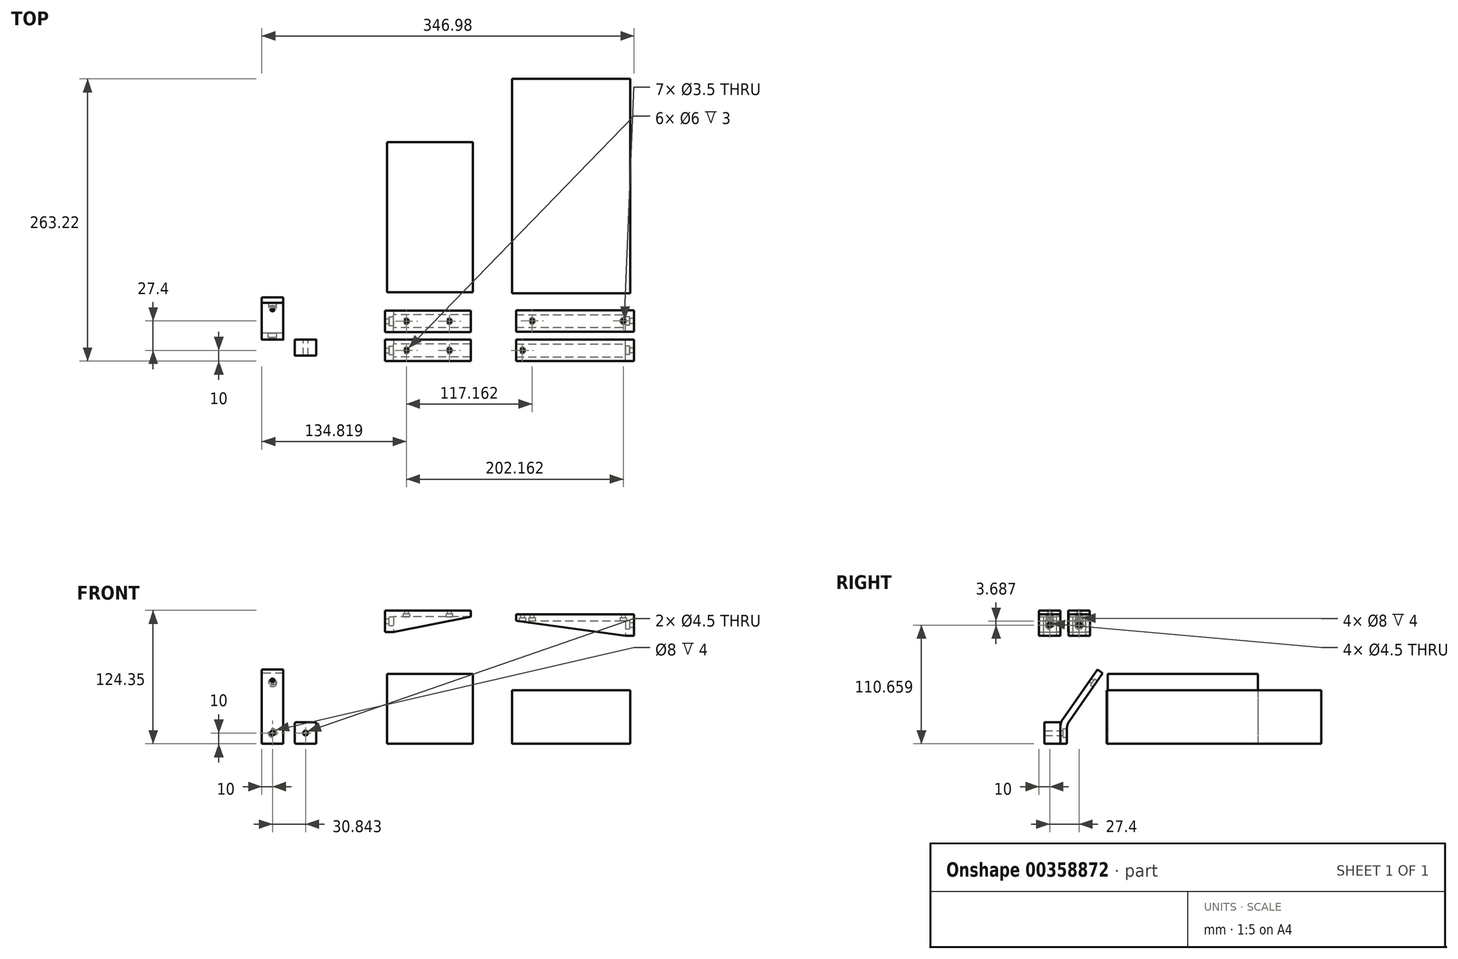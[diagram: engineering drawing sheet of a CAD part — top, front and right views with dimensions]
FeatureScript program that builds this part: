
annotation { "Feature Type Name" : "Feature", "Feature Type Description" : "" }
export const myFeature = defineFeature(function(context is Context, id is Id, definition is map)
    precondition{}
    {
        {
            var Q0;
            Q0=qCreatedBy(makeId("Right.planeOp"),FACE);
            var sketch = newSketch(context, id + "F0", { "sketchPlane" : qUnion([Q0])});
            skLineSegment(sketch, "E0", {"start": v(0, 0) * mm, "end": v(6, 0) * mm});
            skLineSegment(sketch, "E1", {"start": v(6, 0) * mm, "end": v(6, 18.1) * mm});
            skLineSegment(sketch, "E2", {"start": v(6, 18.1) * mm, "end": v(39.33, 65.7) * mm});
            skLineSegment(sketch, "E3", {"start": v(39.33, 65.7) * mm, "end": v(34.41, 69.15) * mm});
            skLineSegment(sketch, "E4", {"start": v(34.41, 69.15) * mm, "end": v(0, 20) * mm});
            skLineSegment(sketch, "E5", {"start": v(0, 20) * mm, "end": v(0, 0) * mm});
            skSolve(sketch);
        }
        {
            var Q0;
            Q0=makeQuery(id+"F0.imprint","IMPRINT",FACE,{"disambiguationData":[TD([[makeQuery(id+"F0.imprint","IMPRINT",EDGE,{"derivedFrom":sQuery(id+"F0.wireOp",EDGE,"E0")}),1.0]])]});
            extrude(context, id + "F1", {"entities" : qUnion([Q0]), "depth" : 20 * mm});
        }
        {
            var Q0;
            Q0=makeQuery(id+"F1.opExtrude","SWEPT_FACE",FACE,{"disambiguationData":[OSD([sQuery(id+"F0.wireOp",EDGE,"E1")])]});
            var sketch = newSketch(context, id + "F2", { "sketchPlane" : qUnion([Q0])});
            skCircle(sketch, "E6", {"center": v(-10, 10) * mm, "radius": 2.25 * mm});
            skPoint(sketch, "E6.centerSnap0", {"position": v(-10, 0) * mm});
            skCircle(sketch, "E7", {"center": v(-10, 10) * mm, "radius": 4 * mm});
            skSolve(sketch);
        }
        {
            var Q0;
            Q0=makeQuery(id+"F1.opExtrude","SWEPT_FACE",FACE,{"disambiguationData":[OSD([sQuery(id+"F0.wireOp",EDGE,"E4")])]});
            var sketch = newSketch(context, id + "F3", { "sketchPlane" : qUnion([Q0])});
            skCircle(sketch, "E8", {"center": v(10, 64.38) * mm, "radius": 1.75 * mm});
            skPoint(sketch, "E8.centerSnap0", {"position": v(10, 16.38) * mm});
            skCircle(sketch, "E9", {"center": v(10, 64.38) * mm, "radius": 3.5 * mm});
            skSolve(sketch);
        }
        {
            var Q0;
            Q0=makeQuery(id+"F3.imprint","IMPRINT",FACE,{"disambiguationData":[TD([[makeQuery(id+"F3.imprint","IMPRINT",EDGE,{"derivedFrom":sQuery(id+"F3.wireOp",EDGE,"E8")}),1.0]])]});
            extrude(context, id + "F4", {"entities" : qUnion([Q0]), "operationType" : NewBodyOperationType.REMOVE, "oppositeDirection" : true, "depth" : 25 * mm});
        }
        {
            var Q0;
            Q0=makeQuery(id+"F1.opExtrude","SWEPT_FACE",FACE,{"disambiguationData":[OSD([sQuery(id+"F0.wireOp",EDGE,"E2")])]});
            var sketch = newSketch(context, id + "F5", { "sketchPlane" : qUnion([Q0])});
            skCircle(sketch, "E10", {"center": v(-10, 64.38) * mm, "radius": 3.5 * mm});
            skSolve(sketch);
        }
        {
            var Q0;
            Q0=makeQuery(id+"F5.imprint","IMPRINT",FACE,{"disambiguationData":[TD([[makeQuery(id+"F5.imprint","IMPRINT",EDGE,{"derivedFrom":sQuery(id+"F5.wireOp",EDGE,"E10")}),1.0]])]});
            extrude(context, id + "F6", {"entities" : qUnion([Q0]), "operationType" : NewBodyOperationType.REMOVE, "oppositeDirection" : true, "depth" : 3 * mm});
        }
        {
            var Q0;
            Q0=makeQuery(id+"F2.imprint","IMPRINT",FACE,{"disambiguationData":[TD([[makeQuery(id+"F2.imprint","IMPRINT",EDGE,{"derivedFrom":sQuery(id+"F2.wireOp",EDGE,"E6")}),1.0]])]});
            extrude(context, id + "F7", {"entities" : qUnion([Q0]), "operationType" : NewBodyOperationType.REMOVE, "oppositeDirection" : true, "depth" : 25 * mm});
        }
        {
            var Q0;
            Q0=makeQuery(id+"F2.imprint","IMPRINT",FACE,{"disambiguationData":[TD([[makeQuery(id+"F2.imprint","IMPRINT",EDGE,{"derivedFrom":sQuery(id+"F2.wireOp",EDGE,"E6")}),-1.0]])]});
            extrude(context, id + "F8", {"entities" : qUnion([Q0]), "operationType" : NewBodyOperationType.REMOVE, "oppositeDirection" : true, "depth" : 4 * mm});
        }
        {
            var Q0;
            Q0=makeQuery(id+"F1.opExtrude","SWEPT_EDGE",EDGE,{"disambiguationData":[OSD([sQuery(id+"F0.wireOp",EDGE,"E1"),sQuery(id+"F0.wireOp",EDGE,"E2")])]});
            var Q1;
            Q1=makeQuery(id+"F1.opExtrude","SWEPT_EDGE",EDGE,{"disambiguationData":[OSD([sQuery(id+"F0.wireOp",EDGE,"E4"),sQuery(id+"F0.wireOp",EDGE,"E5")])]});
            fillet(context, id + "F9", {"entities" : qUnion([Q0, Q1]), "radius" : 13 * mm, "tangentPropagation" : true, "allowEdgeOverflow" : false});
        }
        {
            var Q0;
            Q0=qCreatedBy(makeId("Top.planeOp"),FACE);
            var sketch = newSketch(context, id + "F10", { "sketchPlane" : qUnion([Q0])});
            skLineSegment(sketch, "E11.bottom", {"start": v(116.68, 184.13) * mm, "end": v(196.68, 184.13) * mm});
            skLineSegment(sketch, "E11.top", {"start": v(116.68, 44.13) * mm, "end": v(196.68, 44.13) * mm});
            skLineSegment(sketch, "E11.left", {"start": v(116.68, 184.13) * mm, "end": v(116.68, 44.13) * mm});
            skLineSegment(sketch, "E11.right", {"start": v(196.68, 184.13) * mm, "end": v(196.68, 44.13) * mm});
            skSolve(sketch);
        }
        {
            var Q0;
            Q0=makeQuery(id+"F10.imprint","IMPRINT",FACE,{"disambiguationData":[TD([[makeQuery(id+"F10.imprint","IMPRINT",EDGE,{"derivedFrom":sQuery(id+"F10.wireOp",EDGE,"E11.bottom")}),-1.0]])]});
            extrude(context, id + "F11", {"entities" : qUnion([Q0]), "depth" : 65 * mm});
        }
        {
            var Q0;
            Q0=qCreatedBy(makeId("Top.planeOp"),FACE);
            var sketch = newSketch(context, id + "F12", { "sketchPlane" : qUnion([Q0])});
            skLineSegment(sketch, "E12.bottom", {"start": v(233.36, 43.22) * mm, "end": v(343.36, 43.22) * mm});
            skLineSegment(sketch, "E12.top", {"start": v(233.36, 243.22) * mm, "end": v(343.36, 243.22) * mm});
            skLineSegment(sketch, "E12.left", {"start": v(233.36, 43.22) * mm, "end": v(233.36, 243.22) * mm});
            skLineSegment(sketch, "E12.right", {"start": v(343.36, 43.22) * mm, "end": v(343.36, 243.22) * mm});
            skSolve(sketch);
        }
        {
            var Q0;
            Q0=makeQuery(id+"F12.imprint","IMPRINT",FACE,{"disambiguationData":[TD([[makeQuery(id+"F12.imprint","IMPRINT",EDGE,{"derivedFrom":sQuery(id+"F12.wireOp",EDGE,"E12.bottom")}),1.0]])]});
            extrude(context, id + "F13", {"entities" : qUnion([Q0]), "depth" : 50 * mm});
        }
        {
            var Q0;
            Q0=qCreatedBy(makeId("Front.planeOp"),FACE);
            var sketch = newSketch(context, id + "F14", { "sketchPlane" : qUnion([Q0])});
            skLineSegment(sketch, "E13", {"start": v(114.82, 104.35) * mm, "end": v(122.82, 104.35) * mm});
            skLineSegment(sketch, "E14", {"start": v(114.82, 104.35) * mm, "end": v(114.82, 124.35) * mm});
            skLineSegment(sketch, "E15", {"start": v(114.82, 124.35) * mm, "end": v(194.82, 124.35) * mm});
            skLineSegment(sketch, "E16", {"start": v(194.82, 124.35) * mm, "end": v(194.82, 118.35) * mm});
            skLineSegment(sketch, "E17", {"start": v(194.82, 118.35) * mm, "end": v(122.82, 118.35) * mm});
            skLineSegment(sketch, "E18", {"start": v(122.82, 118.35) * mm, "end": v(122.82, 104.35) * mm});
            skSolve(sketch);
        }
        {
            var Q0;
            Q0=makeQuery(id+"F14.imprint","IMPRINT",FACE,{"disambiguationData":[TD([[makeQuery(id+"F14.imprint","IMPRINT",EDGE,{"derivedFrom":sQuery(id+"F14.wireOp",EDGE,"E13")}),1.0]])]});
            extrude(context, id + "F15", {"entities" : qUnion([Q0]), "depth" : 20 * mm});
        }
        {
            var Q0;
            Q0=makeQuery(id+"F15.opExtrude","SWEPT_FACE",FACE,{"disambiguationData":[OSD([sQuery(id+"F14.wireOp",EDGE,"E18")])]});
            var sketch = newSketch(context, id + "F16", { "sketchPlane" : qUnion([Q0])});
            skCircle(sketch, "E19", {"center": v(-10, 114.35) * mm, "radius": 2.25 * mm});
            skPoint(sketch, "E19.centerSnap0", {"position": v(-10, 104.35) * mm});
            skCircle(sketch, "E20", {"center": v(-10, 114.35) * mm, "radius": 4 * mm});
            skSolve(sketch);
        }
        {
            var Q0;
            Q0=makeQuery(id+"F16.imprint","IMPRINT",FACE,{"disambiguationData":[TD([[makeQuery(id+"F16.imprint","IMPRINT",EDGE,{"derivedFrom":sQuery(id+"F16.wireOp",EDGE,"E19")}),1.0]])]});
            extrude(context, id + "F17", {"entities" : qUnion([Q0]), "operationType" : NewBodyOperationType.REMOVE, "endBound" : BoundingType.THROUGH_ALL, "oppositeDirection" : true, "depth" : 25 * mm});
        }
        {
            var Q0;
            Q0=makeQuery(id+"F16.imprint","IMPRINT",FACE,{"disambiguationData":[TD([[makeQuery(id+"F16.imprint","IMPRINT",EDGE,{"derivedFrom":sQuery(id+"F16.wireOp",EDGE,"E19")}),-1.0]])]});
            extrude(context, id + "F18", {"entities" : qUnion([Q0]), "operationType" : NewBodyOperationType.REMOVE, "oppositeDirection" : true, "depth" : 4 * mm});
        }
        {
            var Q0;
            Q0=makeQuery(id+"F15.opExtrude","CAP_VERTEX",VERTEX,{"disambiguationData":[OSD([sQuery(id+"F14.wireOp",EDGE,"E13"),sQuery(id+"F14.wireOp",EDGE,"E18")])],"isStart":false});
            var Q1;
            Q1=makeQuery(id+"F15.opExtrude","CAP_VERTEX",VERTEX,{"disambiguationData":[OSD([sQuery(id+"F14.wireOp",EDGE,"E13"),sQuery(id+"F14.wireOp",EDGE,"E18")])],"isStart":true});
            var Q2;
            Q2=makeQuery(id+"F15.opExtrude","CAP_VERTEX",VERTEX,{"disambiguationData":[OSD([sQuery(id+"F14.wireOp",EDGE,"E16"),sQuery(id+"F14.wireOp",EDGE,"E17")])],"isStart":false});
            cPlane(context, id + "F19", {"entities" : qUnion([Q0, Q1, Q2]), "cplaneType" : CPlaneType.THREE_POINT, "offset" : 25 * mm, "width" : 150 * mm, "height" : 150 * mm});
        }
        {
            var Q0;
            Q0=qCreatedBy(id+"F19.planeOp",FACE);
            var sketch = newSketch(context, id + "F20", { "sketchPlane" : qUnion([Q0])});
            skLineSegment(sketch, "E21.bottom", {"start": v(140.48, -20) * mm, "end": v(213.83, -20) * mm});
            skLineSegment(sketch, "E21.top", {"start": v(140.48, -16) * mm, "end": v(213.83, -16) * mm});
            skLineSegment(sketch, "E21.left", {"start": v(140.48, -20) * mm, "end": v(140.48, -16) * mm});
            skLineSegment(sketch, "E21.right", {"start": v(213.83, -20) * mm, "end": v(213.83, -16) * mm});
            skLineSegment(sketch, "E22.bottom", {"start": v(140.48, 0) * mm, "end": v(213.83, 0) * mm});
            skLineSegment(sketch, "E22.top", {"start": v(140.48, -4) * mm, "end": v(213.83, -4) * mm});
            skLineSegment(sketch, "E22.left", {"start": v(140.48, 0) * mm, "end": v(140.48, -4) * mm});
            skLineSegment(sketch, "E22.right", {"start": v(213.83, 0) * mm, "end": v(213.83, -4) * mm});
            skSolve(sketch);
        }
        {
            var Q0;
            Q0=qSketchRegion(id+"F20",true);
            extrude(context, id + "F21", {"entities" : qUnion([Q0]), "operationType" : NewBodyOperationType.ADD, "endBound" : BoundingType.UP_TO_NEXT, "depth" : 25 * mm});
        }
        {
            var Q0;
            Q0=makeQuery(id+"F15.opExtrude","SWEPT_FACE",FACE,{"disambiguationData":[OSD([sQuery(id+"F14.wireOp",EDGE,"E17")])]});
            var sketch = newSketch(context, id + "F22", { "sketchPlane" : qUnion([Q0])});
            skCircle(sketch, "E23", {"center": v(174.82, 10) * mm, "radius": 1.75 * mm});
            skPoint(sketch, "E23.centerSnap0", {"position": v(194.82, 10) * mm});
            skCircle(sketch, "E24", {"center": v(174.82, 10) * mm, "radius": 3 * mm});
            skCircle(sketch, "E25", {"center": v(134.82, 10) * mm, "radius": 1.75 * mm});
            skCircle(sketch, "E26", {"center": v(134.82, 10) * mm, "radius": 3 * mm});
            skSolve(sketch);
        }
        {
            var Q0;
            Q0=makeQuery(id+"F22.imprint","IMPRINT",FACE,{"disambiguationData":[TD([[makeQuery(id+"F22.imprint","IMPRINT",EDGE,{"derivedFrom":sQuery(id+"F22.wireOp",EDGE,"E25")}),1.0]])]});
            var Q1;
            Q1=makeQuery(id+"F22.imprint","IMPRINT",FACE,{"disambiguationData":[TD([[makeQuery(id+"F22.imprint","IMPRINT",EDGE,{"derivedFrom":sQuery(id+"F22.wireOp",EDGE,"E23")}),1.0]])]});
            extrude(context, id + "F23", {"entities" : qUnion([Q0, Q1]), "operationType" : NewBodyOperationType.REMOVE, "endBound" : BoundingType.THROUGH_ALL, "oppositeDirection" : true, "depth" : 25 * mm});
        }
        {
            var Q0;
            Q0=makeQuery(id+"F22.imprint","IMPRINT",FACE,{"disambiguationData":[TD([[makeQuery(id+"F22.imprint","IMPRINT",EDGE,{"derivedFrom":sQuery(id+"F22.wireOp",EDGE,"E25")}),-1.0]])]});
            var Q1;
            Q1=makeQuery(id+"F22.imprint","IMPRINT",FACE,{"disambiguationData":[TD([[makeQuery(id+"F22.imprint","IMPRINT",EDGE,{"derivedFrom":sQuery(id+"F22.wireOp",EDGE,"E23")}),-1.0]])]});
            extrude(context, id + "F24", {"entities" : qUnion([Q0, Q1]), "operationType" : NewBodyOperationType.REMOVE, "oppositeDirection" : true, "depth" : 3 * mm});
        }
        {
            var Q0;
            Q0=qCreatedBy(makeId("Front.planeOp"),FACE);
            var sketch = newSketch(context, id + "F25", { "sketchPlane" : qUnion([Q0])});
            skLineSegment(sketch, "E27", {"start": v(338.98, 100.66) * mm, "end": v(346.98, 100.66) * mm});
            skLineSegment(sketch, "E28", {"start": v(346.98, 100.66) * mm, "end": v(346.98, 120.66) * mm});
            skLineSegment(sketch, "E29", {"start": v(346.98, 120.66) * mm, "end": v(236.98, 120.66) * mm});
            skLineSegment(sketch, "E30", {"start": v(236.98, 120.66) * mm, "end": v(236.98, 114.66) * mm});
            skLineSegment(sketch, "E31", {"start": v(236.98, 114.66) * mm, "end": v(338.98, 114.66) * mm});
            skLineSegment(sketch, "E32", {"start": v(338.98, 114.66) * mm, "end": v(338.98, 100.66) * mm});
            skSolve(sketch);
        }
        {
            var Q0;
            Q0=makeQuery(id+"F25.imprint","IMPRINT",FACE,{"disambiguationData":[TD([[makeQuery(id+"F25.imprint","IMPRINT",EDGE,{"derivedFrom":sQuery(id+"F25.wireOp",EDGE,"E27")}),1.0]])]});
            extrude(context, id + "F26", {"entities" : qUnion([Q0]), "depth" : 20 * mm});
        }
        {
            var Q0;
            Q0=makeQuery(id+"F26.opExtrude","SWEPT_FACE",FACE,{"disambiguationData":[OSD([sQuery(id+"F25.wireOp",EDGE,"E32")])]});
            var sketch = newSketch(context, id + "F27", { "sketchPlane" : qUnion([Q0])});
            skCircle(sketch, "E33", {"center": v(10, 110.66) * mm, "radius": 2.25 * mm});
            skPoint(sketch, "E33.centerSnap0", {"position": v(10, 100.66) * mm});
            skCircle(sketch, "E34", {"center": v(10, 110.66) * mm, "radius": 4 * mm});
            skSolve(sketch);
        }
        {
            var Q0;
            Q0=makeQuery(id+"F27.imprint","IMPRINT",FACE,{"disambiguationData":[TD([[makeQuery(id+"F27.imprint","IMPRINT",EDGE,{"derivedFrom":sQuery(id+"F27.wireOp",EDGE,"E33")}),-1.0]])]});
            extrude(context, id + "F28", {"entities" : qUnion([Q0]), "operationType" : NewBodyOperationType.REMOVE, "oppositeDirection" : true, "depth" : 4 * mm});
        }
        {
            var Q0;
            Q0=makeQuery(id+"F28.boolean.opBoolean","SPLIT",FACE,{"disambiguationData":[TD([makeQuery(id+"F28.opExtrude","SWEPT_FACE",FACE,{"disambiguationData":[OSD([sQuery(id+"F27.wireOp",EDGE,"E33")])]})])],"derivedFrom":makeQuery(id+"F26.opExtrude","SWEPT_FACE",FACE,{"disambiguationData":[OSD([sQuery(id+"F25.wireOp",EDGE,"E32")])]})});
            extrude(context, id + "F29", {"entities" : qUnion([Q0]), "operationType" : NewBodyOperationType.REMOVE, "endBound" : BoundingType.THROUGH_ALL, "oppositeDirection" : true, "depth" : 25 * mm});
        }
        {
            var Q0;
            Q0=makeQuery(id+"F26.opExtrude","CAP_VERTEX",VERTEX,{"disambiguationData":[OSD([sQuery(id+"F25.wireOp",EDGE,"E30"),sQuery(id+"F25.wireOp",EDGE,"E31")])],"isStart":false});
            var Q1;
            Q1=makeQuery(id+"F26.opExtrude","CAP_VERTEX",VERTEX,{"disambiguationData":[OSD([sQuery(id+"F25.wireOp",EDGE,"E30"),sQuery(id+"F25.wireOp",EDGE,"E31")])],"isStart":true});
            var Q2;
            Q2=makeQuery(id+"F26.opExtrude","CAP_VERTEX",VERTEX,{"disambiguationData":[OSD([sQuery(id+"F25.wireOp",EDGE,"E27"),sQuery(id+"F25.wireOp",EDGE,"E32")])],"isStart":false});
            cPlane(context, id + "F30", {"entities" : qUnion([Q0, Q1, Q2]), "cplaneType" : CPlaneType.THREE_POINT, "offset" : 25 * mm, "width" : 150 * mm, "height" : 150 * mm});
        }
        {
            var Q0;
            Q0=qCreatedBy(id+"F30.planeOp",FACE);
            var sketch = newSketch(context, id + "F31", { "sketchPlane" : qUnion([Q0])});
            skLineSegment(sketch, "E35.bottom", {"start": v(219.19, -20) * mm, "end": v(322.14, -20) * mm});
            skLineSegment(sketch, "E35.top", {"start": v(219.19, -16) * mm, "end": v(322.14, -16) * mm});
            skLineSegment(sketch, "E35.left", {"start": v(219.19, -20) * mm, "end": v(219.19, -16) * mm});
            skLineSegment(sketch, "E35.right", {"start": v(322.14, -20) * mm, "end": v(322.14, -16) * mm});
            skLineSegment(sketch, "E36.bottom", {"start": v(219.19, -4) * mm, "end": v(322.14, -4) * mm});
            skLineSegment(sketch, "E36.top", {"start": v(219.19, 0) * mm, "end": v(322.14, 0) * mm});
            skLineSegment(sketch, "E36.left", {"start": v(219.19, -4) * mm, "end": v(219.19, 0) * mm});
            skLineSegment(sketch, "E36.right", {"start": v(322.14, -4) * mm, "end": v(322.14, 0) * mm});
            skSolve(sketch);
        }
        {
            var Q0;
            Q0=makeQuery(id+"F31.imprint","IMPRINT",FACE,{"disambiguationData":[TD([[makeQuery(id+"F31.imprint","IMPRINT",EDGE,{"derivedFrom":sQuery(id+"F31.wireOp",EDGE,"E35.bottom")}),1.0]])]});
            var Q1;
            Q1=makeQuery(id+"F31.imprint","IMPRINT",FACE,{"disambiguationData":[TD([[makeQuery(id+"F31.imprint","IMPRINT",EDGE,{"derivedFrom":sQuery(id+"F31.wireOp",EDGE,"E36.bottom")}),1.0]])]});
            extrude(context, id + "F32", {"entities" : qUnion([Q0, Q1]), "operationType" : NewBodyOperationType.ADD, "endBound" : BoundingType.UP_TO_NEXT, "depth" : 25 * mm});
        }
        {
            var Q0;
            Q0=makeQuery(id+"F26.opExtrude","SWEPT_BODY",BODY,{"disambiguationData":[OSD([sQuery(id+"F25.wireOp",EDGE,"E27"),sQuery(id+"F25.wireOp",EDGE,"E28"),sQuery(id+"F25.wireOp",EDGE,"E29"),sQuery(id+"F25.wireOp",EDGE,"E30"),sQuery(id+"F25.wireOp",EDGE,"E31"),sQuery(id+"F25.wireOp",EDGE,"E32")])]});
            transform(context, id + "F33", {"entities" : qUnion([Q0]), "transformType" : TransformType.TRANSLATION_3D, "dx" : 0 * mm, "dy" : 27.4 * mm, "dz" : 0 * mm, "makeCopy" : true});
        }
        {
            var Q0;
            Q0=makeQuery(id+"F26.opExtrude","SWEPT_FACE",FACE,{"disambiguationData":[OSD([sQuery(id+"F25.wireOp",EDGE,"E31")])]});
            var sketch = newSketch(context, id + "F34", { "sketchPlane" : qUnion([Q0])});
            skCircle(sketch, "E37", {"center": v(242.98, 10) * mm, "radius": 1.75 * mm});
            skPoint(sketch, "E37.centerSnap0", {"position": v(236.98, 10) * mm});
            skCircle(sketch, "E38", {"center": v(242.98, 10) * mm, "radius": 3 * mm});
            skSolve(sketch);
        }
        {
            var Q0;
            Q0=makeQuery(id+"F33.opPattern","COPY",FACE,{"derivedFrom":makeQuery(id+"F26.opExtrude","SWEPT_FACE",FACE,{"disambiguationData":[OSD([sQuery(id+"F25.wireOp",EDGE,"E31")])]}),"instanceName":"1"});
            var sketch = newSketch(context, id + "F35", { "sketchPlane" : qUnion([Q0])});
            skCircle(sketch, "E39", {"center": v(251.98, -17.4) * mm, "radius": 1.75 * mm});
            skPoint(sketch, "E39.centerSnap0", {"position": v(236.98, -17.4) * mm});
            skCircle(sketch, "E40", {"center": v(251.98, -17.4) * mm, "radius": 3 * mm});
            skCircle(sketch, "E41", {"center": v(336.98, -17.4) * mm, "radius": 1.75 * mm});
            skCircle(sketch, "E42", {"center": v(336.98, -17.4) * mm, "radius": 3 * mm});
            skSolve(sketch);
        }
        {
            var Q0;
            Q0=makeQuery(id+"F34.imprint","IMPRINT",FACE,{"disambiguationData":[TD([[makeQuery(id+"F34.imprint","IMPRINT",EDGE,{"derivedFrom":sQuery(id+"F34.wireOp",EDGE,"E37")}),-1.0]])]});
            var Q1;
            Q1=makeQuery(id+"F35.imprint","IMPRINT",FACE,{"disambiguationData":[TD([[makeQuery(id+"F35.imprint","IMPRINT",EDGE,{"derivedFrom":sQuery(id+"F35.wireOp",EDGE,"E39")}),-1.0]])]});
            var Q2;
            Q2=makeQuery(id+"F35.imprint","IMPRINT",FACE,{"disambiguationData":[TD([[makeQuery(id+"F35.imprint","IMPRINT",EDGE,{"derivedFrom":sQuery(id+"F35.wireOp",EDGE,"E41")}),-1.0]])]});
            extrude(context, id + "F36", {"entities" : qUnion([Q0, Q1, Q2]), "operationType" : NewBodyOperationType.REMOVE, "oppositeDirection" : true, "depth" : 3 * mm});
        }
        {
            var Q0;
            Q0=makeQuery(id+"F36.boolean.opBoolean","SPLIT",FACE,{"disambiguationData":[TD([makeQuery(id+"F36.opExtrude","SWEPT_FACE",FACE,{"disambiguationData":[OSD([sQuery(id+"F34.wireOp",EDGE,"E37")])]})])],"derivedFrom":makeQuery(id+"F26.opExtrude","SWEPT_FACE",FACE,{"disambiguationData":[OSD([sQuery(id+"F25.wireOp",EDGE,"E31")])]})});
            var Q1;
            Q1=makeQuery(id+"F36.boolean.opBoolean","SPLIT",FACE,{"disambiguationData":[TD([makeQuery(id+"F36.opExtrude","SWEPT_FACE",FACE,{"disambiguationData":[OSD([sQuery(id+"F35.wireOp",EDGE,"E39")])]})])],"derivedFrom":makeQuery(id+"F33.opPattern","COPY",FACE,{"derivedFrom":makeQuery(id+"F26.opExtrude","SWEPT_FACE",FACE,{"disambiguationData":[OSD([sQuery(id+"F25.wireOp",EDGE,"E31")])]}),"instanceName":"1"})});
            var Q2;
            Q2=makeQuery(id+"F36.boolean.opBoolean","SPLIT",FACE,{"disambiguationData":[TD([makeQuery(id+"F36.opExtrude","SWEPT_FACE",FACE,{"disambiguationData":[OSD([sQuery(id+"F35.wireOp",EDGE,"E41")])]})])],"derivedFrom":makeQuery(id+"F33.opPattern","COPY",FACE,{"derivedFrom":makeQuery(id+"F26.opExtrude","SWEPT_FACE",FACE,{"disambiguationData":[OSD([sQuery(id+"F25.wireOp",EDGE,"E31")])]}),"instanceName":"1"})});
            extrude(context, id + "F37", {"entities" : qUnion([Q0, Q1, Q2]), "operationType" : NewBodyOperationType.REMOVE, "endBound" : BoundingType.THROUGH_ALL, "oppositeDirection" : true, "depth" : 25 * mm});
        }
        {
            var Q0;
            {var subQ0=sQuery(id+"F35.wireOp",EDGE,"E42");var subQ1=sQuery(id+"F25.wireOp",EDGE,"E32");var subQ2=sQuery(id+"F25.wireOp",EDGE,"E31");var subQ3=sQuery(id+"F25.wireOp",EDGE,"E30");var subQ4=sQuery(id+"F25.wireOp",EDGE,"E29");var subQ5=sQuery(id+"F25.wireOp",EDGE,"E28");var subQ6=sQuery(id+"F25.wireOp",EDGE,"E27");var subQ10=makeQuery(id+"F26.opExtrude","SWEPT_EDGE",EDGE,{"disambiguationData":[OSD([subQ2,subQ1])]});var subQ11=makeQuery(id+"F33.opPattern","COPY",EDGE,{"derivedFrom":makeQuery(id+"F28.boolean.opBoolean","SPLIT",EDGE,{"disambiguationData":[TD([makeQuery(id+"F26.opExtrude","CAP_FACE",FACE,{"disambiguationData":[OSD([subQ6,subQ5,subQ4,subQ3,subQ2,subQ1])],"isStart":true})])],"derivedFrom":subQ10}),"instanceName":"1"});var subQ12=makeQuery(id+"F35.imprint","INTERSECT",VERTEX,{"derivedFrom":[subQ11,subQ0]});Q0=makeQuery(id+"F35.imprint","IMPRINT",FACE,{"disambiguationData":[TD([[makeQuery(id+"F35.imprint","IMPRINT",EDGE,{"disambiguationData":[TD([[subQ12,-1.0]])],"derivedFrom":subQ0}),1.0]])]});}
            extrude(context, id + "F38", {"entities" : qUnion([Q0]), "operationType" : NewBodyOperationType.REMOVE, "oppositeDirection" : true, "depth" : 6 * mm, "symmetric" : true});
        }
        {
            var Q0;
            Q0=makeQuery(id+"F15.opExtrude","SWEPT_BODY",BODY,{"disambiguationData":[OSD([sQuery(id+"F14.wireOp",EDGE,"E13"),sQuery(id+"F14.wireOp",EDGE,"E14"),sQuery(id+"F14.wireOp",EDGE,"E15"),sQuery(id+"F14.wireOp",EDGE,"E16"),sQuery(id+"F14.wireOp",EDGE,"E17"),sQuery(id+"F14.wireOp",EDGE,"E18")])]});
            transform(context, id + "F39", {"entities" : qUnion([Q0]), "transformType" : TransformType.TRANSLATION_3D, "dx" : 0 * mm, "dy" : 27.2 * mm, "dz" : 0 * mm, "makeCopy" : true});
        }
        {
            var Q0;
            Q0=qCreatedBy(makeId("Front.planeOp"),FACE);
            var sketch = newSketch(context, id + "F40", { "sketchPlane" : qUnion([Q0])});
            skLineSegment(sketch, "E43.bottom", {"start": v(30.84, 0) * mm, "end": v(50.84, 0) * mm});
            skLineSegment(sketch, "E43.top", {"start": v(30.84, 20) * mm, "end": v(50.84, 20) * mm});
            skLineSegment(sketch, "E43.left", {"start": v(30.84, 0) * mm, "end": v(30.84, 20) * mm});
            skLineSegment(sketch, "E43.right", {"start": v(50.84, 0) * mm, "end": v(50.84, 20) * mm});
            skCircle(sketch, "E44", {"center": v(40.84, 10) * mm, "radius": 2.25 * mm});
            skPoint(sketch, "E44.centerSnap0", {"position": v(30.84, 10) * mm});
            skPoint(sketch, "E44.centerSnap1", {"position": v(40.84, 0) * mm});
            skSolve(sketch);
        }
        {
            var Q0;
            Q0 = qSketchRegion(id + "F40", true);
            extrude(context, id + "F41", {"entities" : qUnion([Q0]), "depth" : 15 * mm, "offsetDistance" : 25 * mm});
        }
        {
            var Q0;
            Q0=makeQuery(id+"F41.opExtrude","SWEPT_EDGE",EDGE,{"disambiguationData":[OSD([sQuery(id+"F40.wireOp",EDGE,"E43.top"),sQuery(id+"F40.wireOp",EDGE,"E43.right")])]});
            var Q1;
            Q1=makeQuery(id+"F41.opExtrude","SWEPT_EDGE",EDGE,{"disambiguationData":[OSD([sQuery(id+"F40.wireOp",EDGE,"E43.bottom"),sQuery(id+"F40.wireOp",EDGE,"E43.right")])]});
            var Q2;
            Q2=makeQuery(id+"F41.opExtrude","SWEPT_EDGE",EDGE,{"disambiguationData":[OSD([sQuery(id+"F40.wireOp",EDGE,"E43.top"),sQuery(id+"F40.wireOp",EDGE,"E43.left")])]});
            var Q3;
            Q3=makeQuery(id+"F41.opExtrude","SWEPT_EDGE",EDGE,{"disambiguationData":[OSD([sQuery(id+"F40.wireOp",EDGE,"E43.bottom"),sQuery(id+"F40.wireOp",EDGE,"E43.left")])]});
            fillet(context, id + "F42", {"entities" : qUnion([Q0, Q1, Q2, Q3]), "radius" : 1 * mm, "tangentPropagation" : true, "allowEdgeOverflow" : false});
        }
    });
